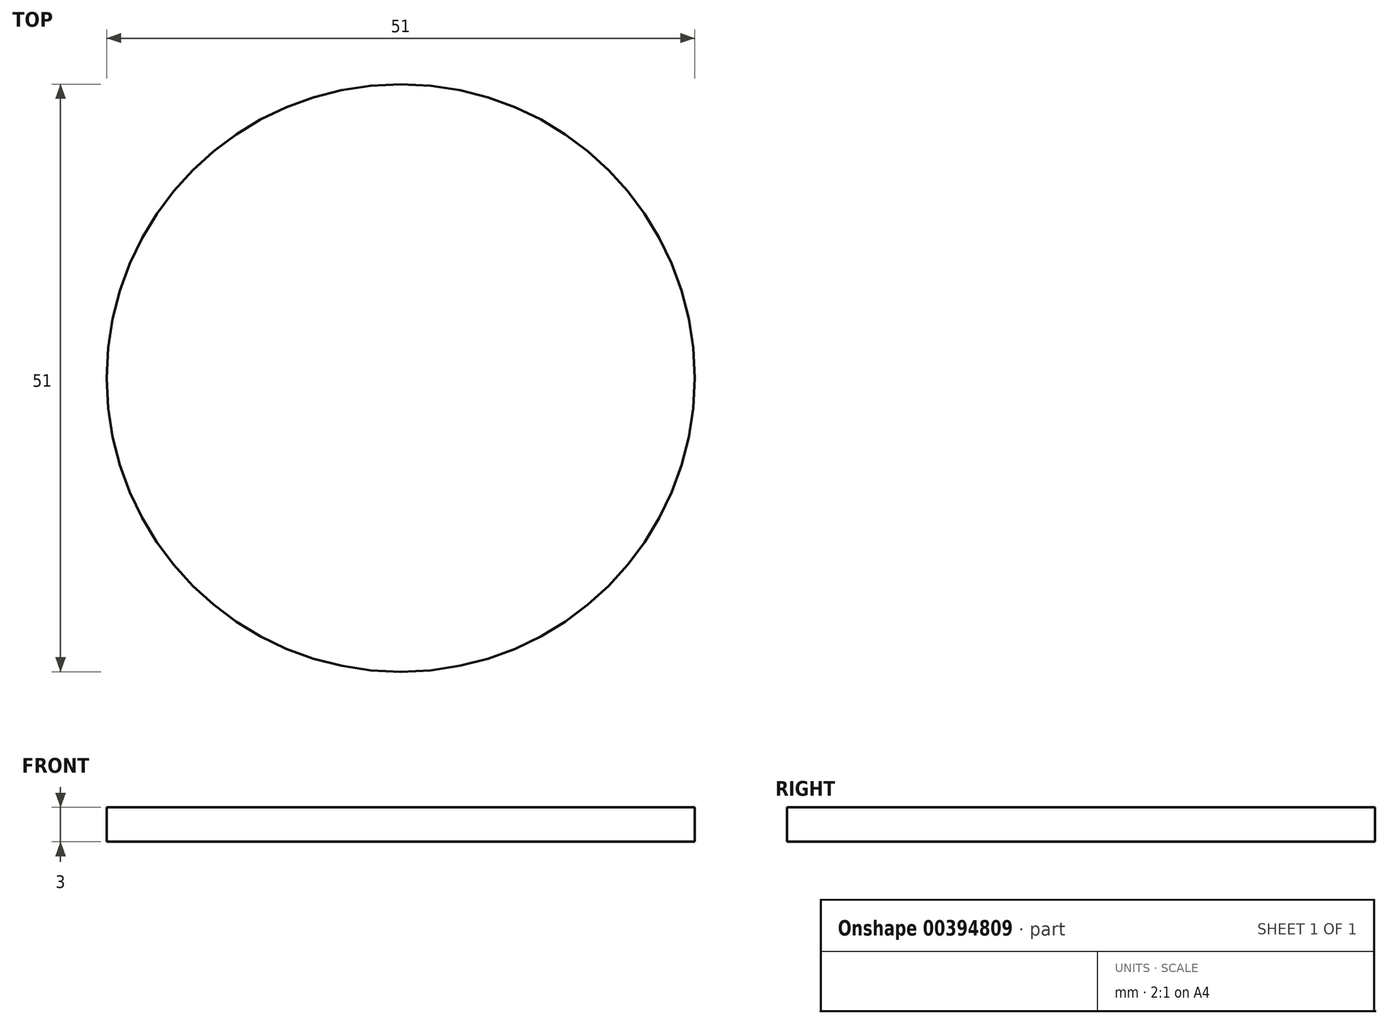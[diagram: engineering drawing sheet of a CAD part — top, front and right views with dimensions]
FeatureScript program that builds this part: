
annotation { "Feature Type Name" : "Feature", "Feature Type Description" : "" }
export const myFeature = defineFeature(function(context is Context, id is Id, definition is map)
    precondition{}
    {
        {
            var Q0;
            Q0=qCreatedBy(makeId("Top.planeOp"),FACE);
            var sketch = newSketch(context, id + "F0", { "sketchPlane" : qUnion([Q0])});
            skCircle(sketch, "E0", {"center": v(0, 0) * mm, "radius": 72 * mm});
            skSolve(sketch);
        }
        {
            var Q0;
            Q0=qSketchRegion(id+"F0",true);
            extrude(context, id + "F1", {"entities" : qUnion([Q0]), "depth" : 3 * mm});
        }
        {
            var Q0;
            Q0=makeQuery(id+"F1.opExtrude","CAP_FACE",FACE,{"disambiguationData":[OSD([sQuery(id+"F0.wireOp",EDGE,"E0")])],"isStart":false});
            var sketch = newSketch(context, id + "F2", { "sketchPlane" : qUnion([Q0])});
            skCircle(sketch, "E1", {"center": v(-40.5, 0) * mm, "radius": 25.5 * mm});
            skLineSegment(sketch, "E2", {"start": v(0, 44.02) * mm, "end": v(0, -38.94) * mm});
            skCircle(sketch, "E3.MirrorC", {"center": v(40.5, 0) * mm, "radius": 25.5 * mm});
            skSolve(sketch);
        }
        {
            var Q0;
            Q0=makeQuery(id+"F2.imprint","IMPRINT",FACE,{"disambiguationData":[TD([[makeQuery(id+"F2.imprint","IMPRINT",EDGE,{"derivedFrom":sQuery(id+"F2.wireOp",EDGE,"E1")}),1.0]])]});
            var Q1;
            Q1=makeQuery(id+"F2.imprint","IMPRINT",FACE,{"disambiguationData":[TD([[makeQuery(id+"F2.imprint","IMPRINT",EDGE,{"derivedFrom":sQuery(id+"F2.wireOp",EDGE,"E3.MirrorC")}),-1.0]])]});
            extrude(context, id + "F3", {"entities" : qUnion([Q0, Q1]), "operationType" : NewBodyOperationType.REMOVE, "oppositeDirection" : true, "depth" : 3 * mm});
        }
        {
            var Q0;
            Q0=makeQuery(id+"F1.opExtrude","CAP_FACE",FACE,{"disambiguationData":[OSD([sQuery(id+"F0.wireOp",EDGE,"E0")])],"isStart":false});
            var sketch = newSketch(context, id + "F4", { "sketchPlane" : qUnion([Q0])});
            skCircle(sketch, "E4", {"center": v(0, 61.5) * mm, "radius": 3 * mm});
            skCircle(sketch, "E5", {"center": v(0, 0) * mm, "radius": 3 * mm});
            skCircle(sketch, "E6.MirrorC", {"center": v(0, -61.5) * mm, "radius": 3 * mm});
            skSolve(sketch);
        }
        {
            var Q0;
            Q0=qSketchRegion(id+"F4",true);
            extrude(context, id + "F5", {"entities" : qUnion([Q0]), "operationType" : NewBodyOperationType.REMOVE, "oppositeDirection" : true, "depth" : 25.4 * mm});
        }
        {
            var Q0;
            Q0=makeQuery(id+"F1.opExtrude","CAP_FACE",FACE,{"disambiguationData":[OSD([sQuery(id+"F0.wireOp",EDGE,"E0")])],"isStart":false});
            var sketch = newSketch(context, id + "F6", { "sketchPlane" : qUnion([Q0])});
            skCircle(sketch, "E7", {"center": v(0, 61.5) * mm, "radius": 3 * mm});
            skCircle(sketch, "E8", {"center": v(0, 0) * mm, "radius": 61.5 * mm, "construction": true});
            skCircle(sketch, "E9.1.0", {"center": v(-53.26, -30.75) * mm, "radius": 3 * mm});
            skCircle(sketch, "E9.2.0", {"center": v(53.26, -30.75) * mm, "radius": 3 * mm});
            skSolve(sketch);
        }
        {
            var Q0;
            Q0=makeQuery(id+"F6.imprint","IMPRINT",FACE,{"disambiguationData":[TD([[makeQuery(id+"F6.imprint","IMPRINT",EDGE,{"derivedFrom":sQuery(id+"F6.wireOp",EDGE,"E9.1.0")}),1.0]])]});
            var Q1;
            Q1=makeQuery(id+"F6.imprint","IMPRINT",FACE,{"disambiguationData":[TD([[makeQuery(id+"F6.imprint","IMPRINT",EDGE,{"derivedFrom":sQuery(id+"F6.wireOp",EDGE,"E9.2.0")}),1.0]])]});
            extrude(context, id + "F7", {"entities" : qUnion([Q0, Q1]), "operationType" : NewBodyOperationType.REMOVE, "oppositeDirection" : true, "depth" : 25.4 * mm});
        }
    });
